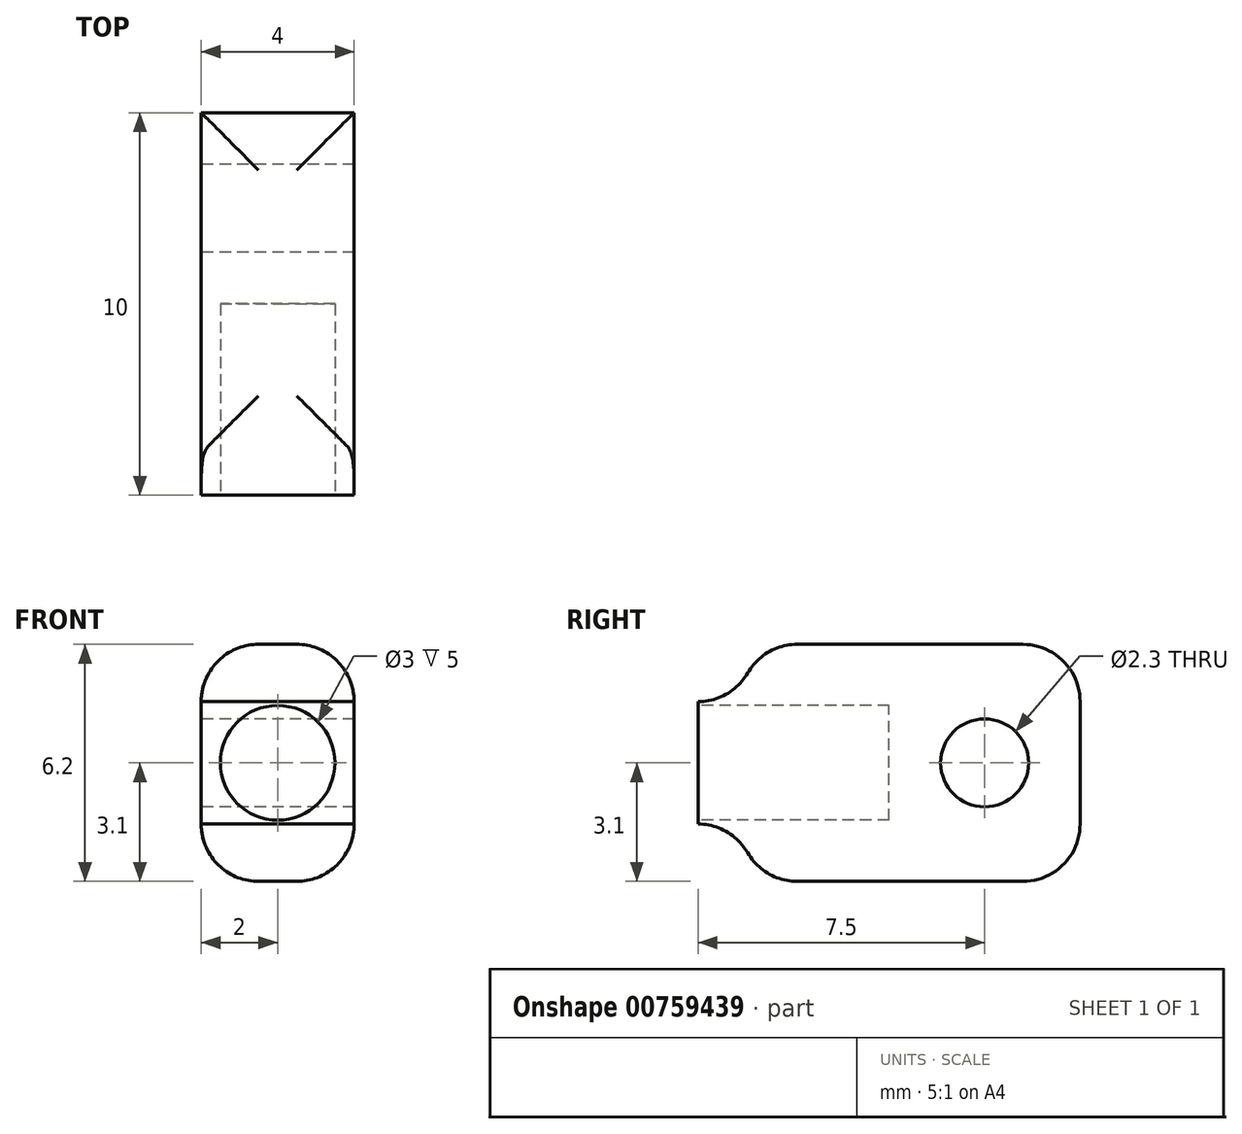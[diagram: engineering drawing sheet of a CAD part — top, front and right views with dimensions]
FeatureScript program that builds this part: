
annotation { "Feature Type Name" : "Feature", "Feature Type Description" : "" }
export const myFeature = defineFeature(function(context is Context, id is Id, definition is map)
    precondition{}
    {
        {
            var Q0;
            Q0=qCreatedBy(makeId("Right.planeOp"),FACE);
            var sketch = newSketch(context, id + "F0", { "sketchPlane" : qUnion([Q0])});
            skLineSegment(sketch, "E0.bottom", {"start": v(5, 3.1) * mm, "end": v(-3.5, 3.1) * mm});
            skLineSegment(sketch, "E0.top", {"start": v(5, -3.1) * mm, "end": v(-3.5, -3.1) * mm});
            skLineSegment(sketch, "E0.left", {"start": v(5, 3.1) * mm, "end": v(5, -3.1) * mm});
            skLineSegment(sketch, "E0.right", {"start": v(-5, 1.6) * mm, "end": v(-5, -1.6) * mm});
            skPoint(sketch, "E0.middle", {"position": v(0, 0) * mm});
            skCircle(sketch, "E1", {"center": v(2.5, 0) * mm, "radius": 1.15 * mm});
            skArc(sketch, "E2", {"start": v(-3.5, 3.1) * mm, "mid": v(-3.94, 2.04) * mm, "end": v(-5, 1.6) * mm});
            skArc(sketch, "E3.MirrorCS", {"start": v(-3.5, -3.1) * mm, "mid": v(-3.94, -2.04) * mm, "end": v(-5, -1.6) * mm});
            skSolve(sketch);
        }
        {
            var Q0;
            Q0 = qSketchRegion(id + "F0", true);
            extrude(context, id + "F1", {"entities" : qUnion([Q0]), "endBound" : BoundingType.SYMMETRIC, "depth" : 4 * mm, "offsetDistance" : 25 * mm});
        }
        {
            var Q0;
            Q0=makeQuery(id+"F1.opExtrude","SWEPT_FACE",FACE,{"disambiguationData":[OSD([sQuery(id+"F0.wireOp",EDGE,"E0.right")])]});
            var sketch = newSketch(context, id + "F2", { "sketchPlane" : qUnion([Q0])});
            skCircle(sketch, "E4", {"center": v(0, 0) * mm, "radius": 1.5 * mm});
            skSolve(sketch);
        }
        {
            var Q0;
            Q0 = qSketchRegion(id + "F2", true);
            extrude(context, id + "F3", {"entities" : qUnion([Q0]), "operationType" : NewBodyOperationType.REMOVE, "oppositeDirection" : true, "depth" : 5 * mm, "offsetDistance" : 25 * mm});
        }
        {
            var Q0;
            Q0=makeQuery(id+"F1.opExtrude","SWEPT_EDGE",EDGE,{"disambiguationData":[OSD([sQuery(id+"F0.wireOp",EDGE,"E0.bottom"),sQuery(id+"F0.wireOp",EDGE,"E2")])]});
            var Q1;
            Q1=makeQuery(id+"F1.opExtrude","SWEPT_EDGE",EDGE,{"disambiguationData":[OSD([sQuery(id+"F0.wireOp",EDGE,"E0.top"),sQuery(id+"F0.wireOp",EDGE,"E3.MirrorCS")])]});
            var Q2;
            Q2=makeQuery(id+"F1.opExtrude","CAP_EDGE",EDGE,{"disambiguationData":[OSD([sQuery(id+"F0.wireOp",EDGE,"E0.top")])],"isStart":false});
            var Q3;
            Q3=makeQuery(id+"F1.opExtrude","CAP_EDGE",EDGE,{"disambiguationData":[OSD([sQuery(id+"F0.wireOp",EDGE,"E0.bottom")])],"isStart":false});
            var Q4;
            Q4=makeQuery(id+"F1.opExtrude","SWEPT_EDGE",EDGE,{"disambiguationData":[OSD([sQuery(id+"F0.wireOp",EDGE,"E0.bottom"),sQuery(id+"F0.wireOp",EDGE,"E0.left")])]});
            var Q5;
            Q5=makeQuery(id+"F1.opExtrude","SWEPT_EDGE",EDGE,{"disambiguationData":[OSD([sQuery(id+"F0.wireOp",EDGE,"E0.top"),sQuery(id+"F0.wireOp",EDGE,"E0.left")])]});
            var Q6;
            Q6=makeQuery(id+"F1.opExtrude","CAP_EDGE",EDGE,{"disambiguationData":[OSD([sQuery(id+"F0.wireOp",EDGE,"E0.bottom")])],"isStart":true});
            var Q7;
            Q7=makeQuery(id+"F1.opExtrude","CAP_EDGE",EDGE,{"disambiguationData":[OSD([sQuery(id+"F0.wireOp",EDGE,"E0.top")])],"isStart":true});
            fillet(context, id + "F4", {"entities" : qUnion([Q0, Q1, Q2, Q3, Q4, Q5, Q6, Q7]), "radius" : 1.5 * mm, "tangentPropagation" : true, "allowEdgeOverflow" : false});
        }
    });
